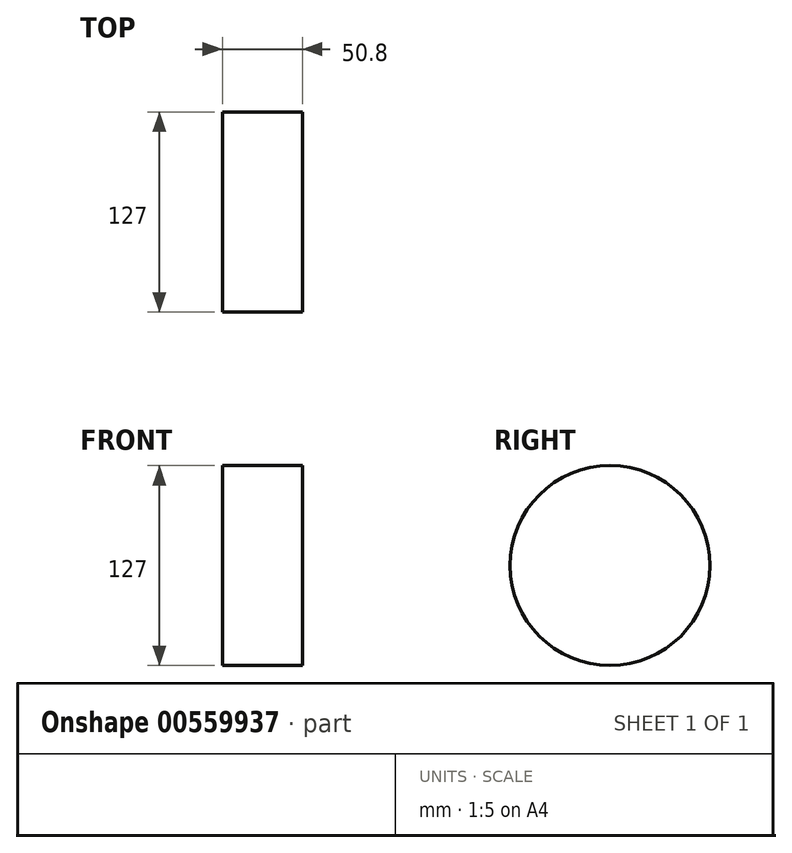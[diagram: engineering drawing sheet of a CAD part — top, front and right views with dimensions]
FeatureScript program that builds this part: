
annotation { "Feature Type Name" : "Feature", "Feature Type Description" : "" }
export const myFeature = defineFeature(function(context is Context, id is Id, definition is map)
    precondition{}
    {
        {
            var Q0;
            Q0=qCreatedBy(makeId("Right.planeOp"),FACE);
            var sketch = newSketch(context, id + "F0", { "sketchPlane" : qUnion([Q0])});
            skCircle(sketch, "E0", {"center": v(0, 0) * mm, "radius": 63.5 * mm});
            skSolve(sketch);
        }
        {
            var Q0;
            Q0=makeQuery(id+"F0.imprint","IMPRINT",FACE,{"disambiguationData":[TD([[makeQuery(id+"F0.imprint","IMPRINT",EDGE,{"derivedFrom":sQuery(id+"F0.wireOp",EDGE,"E0")}),1.0]])]});
            extrude(context, id + "F1", {"entities" : qUnion([Q0]), "depth" : 25.4 * mm, "offsetDistance" : 25.4 * mm, "hasSecondDirection" : true, "secondDirectionOppositeDirection" : true, "secondDirectionDepth" : 25.4 * mm});
        }
    });
